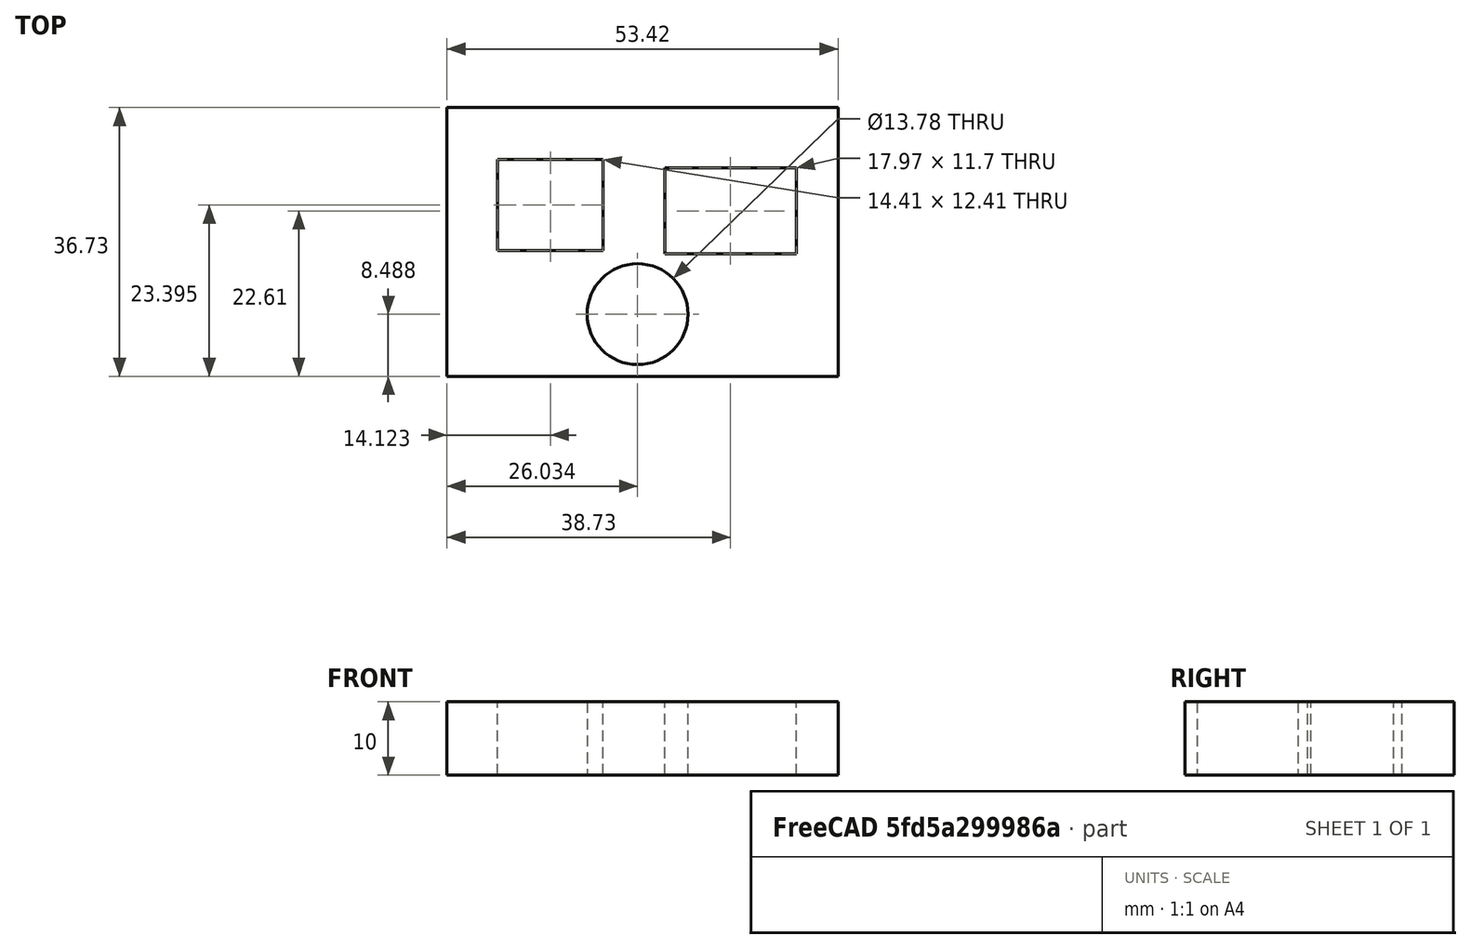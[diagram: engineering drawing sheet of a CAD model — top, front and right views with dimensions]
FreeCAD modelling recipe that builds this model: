
FCSTD DOCUMENT  (FreeCAD 0.20R29410 (Git))
Label: robot_croqueado
License: All rights reserved
LicenseURL: http://en.wikipedia.org/wiki/All_rights_reserved
objects: Sketcher::SketchObject×1, Part::Extrusion×1
note: 2 computed .brp shape members not serialized (recipe doc carries the construction recipe); baked Part::Feature solids carry a one-line shape summary decoded from their .brp

FEATURE [Sketcher::SketchObject] Sketch
  FullyConstrained = false
  sketch-geometry (13):
    g0: LineSegment StartX=0 StartY=36.7332 StartZ=0 EndX=53.4237 EndY=36.7332 EndZ=0
    g1: LineSegment StartX=53.4237 StartY=36.7332 StartZ=0 EndX=53.4237 EndY=0 EndZ=0
    g2: LineSegment StartX=53.4237 StartY=0 StartZ=0 EndX=0 EndY=0 EndZ=0
    g3: LineSegment StartX=0 StartY=0 StartZ=0 EndX=0 EndY=36.7332 EndZ=0
    g4: LineSegment StartX=6.91869 StartY=29.6006 StartZ=0 EndX=21.3267 EndY=29.6006 EndZ=0
    g5: LineSegment StartX=21.3267 StartY=29.6006 StartZ=0 EndX=21.3267 EndY=17.1897 EndZ=0
    g6: LineSegment StartX=21.3267 StartY=17.1897 StartZ=0 EndX=6.91869 EndY=17.1897 EndZ=0
    g7: LineSegment StartX=6.91869 StartY=17.1897 StartZ=0 EndX=6.91869 EndY=29.6006 EndZ=0
    g8: LineSegment StartX=29.7432 StartY=28.4593 StartZ=0 EndX=47.7175 EndY=28.4593 EndZ=0
    g9: LineSegment StartX=47.7175 StartY=28.4593 StartZ=0 EndX=47.7175 EndY=16.7618 EndZ=0
    g10: LineSegment StartX=47.7175 StartY=16.7618 StartZ=0 EndX=29.7432 EndY=16.7618 EndZ=0
    g11: LineSegment StartX=29.7432 StartY=16.7618 StartZ=0 EndX=29.7432 EndY=28.4593 EndZ=0
    g12: Circle CenterX=26.0342 CenterY=8.48787 CenterZ=0 NormalX=0 NormalY=0 NormalZ=1 AngleXU=0 Radius=6.89031
  constraints (26):
    c: Coincident(g0,g1)
    c: Coincident(g1,g2)
    c: Coincident(g2,g3)
    c: Coincident(g3,g0)
    c: Horizontal(g0)
    c: Horizontal(g2)
    c: Vertical(g1)
    c: Vertical(g3)
    c: PointOnObject(g0,g-2)
    c: PointOnObject(g1,g-1)
    c: Coincident(g4,g5)
    c: Coincident(g5,g6)
    c: Coincident(g6,g7)
    c: Coincident(g7,g4)
    c: Horizontal(g4)
    c: Horizontal(g6)
    c: Vertical(g5)
    c: Vertical(g7)
    c: Coincident(g8,g9)
    c: Coincident(g9,g10)
    c: Coincident(g10,g11)
    c: Coincident(g11,g8)
    c: Horizontal(g8)
    c: Horizontal(g10)
    c: Vertical(g9)
    c: Vertical(g11)
FEATURE [Part::Extrusion] Extrude
  Base = -> Sketch
  Dir = (0,0,1)
  DirMode = 2
  FaceMakerClass = Part::FaceMakerBullseye
  LengthFwd = 10
  LengthRev = 0
  Solid = true
  Symmetric = false
